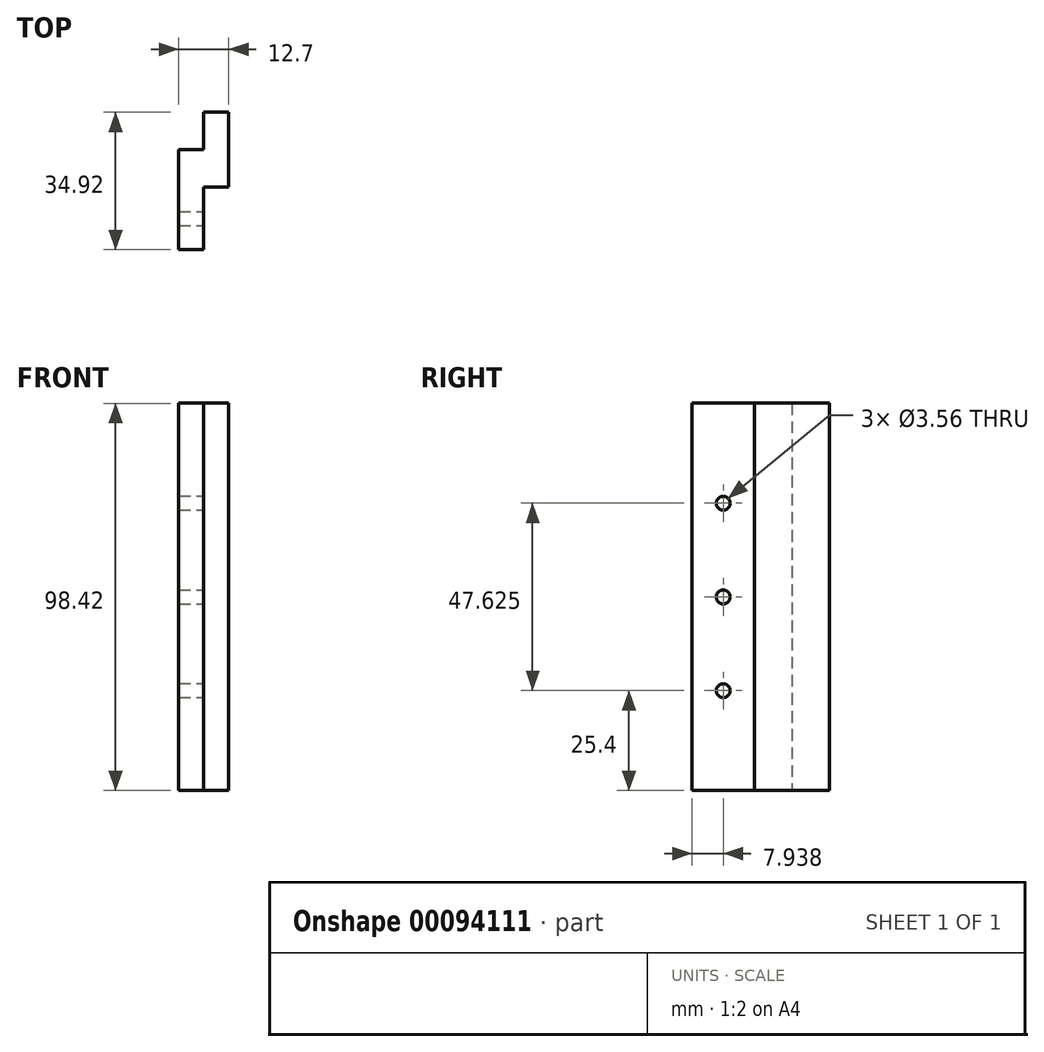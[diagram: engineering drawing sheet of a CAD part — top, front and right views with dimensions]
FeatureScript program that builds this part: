
annotation { "Feature Type Name" : "Feature", "Feature Type Description" : "" }
export const myFeature = defineFeature(function(context is Context, id is Id, definition is map)
    precondition{}
    {
        {
            var Q0;
            Q0=qCreatedBy(makeId("Top.planeOp"),FACE);
            var sketch = newSketch(context, id + "F0", { "sketchPlane" : qUnion([Q0])});
            skLineSegment(sketch, "E0.bottom", {"start": v(0, 0) * mm, "end": v(6.35, 0) * mm});
            skLineSegment(sketch, "E0.top", {"start": v(0, 25.4) * mm, "end": v(6.35, 25.4) * mm});
            skLineSegment(sketch, "E0.left", {"start": v(0, 0) * mm, "end": v(0, 25.4) * mm});
            skLineSegment(sketch, "E0.right", {"start": v(6.35, 0) * mm, "end": v(6.35, 25.4) * mm});
            skLineSegment(sketch, "E1.bottom", {"start": v(6.35, 15.88) * mm, "end": v(12.7, 15.88) * mm});
            skLineSegment(sketch, "E1.top", {"start": v(6.35, 34.93) * mm, "end": v(12.7, 34.93) * mm});
            skLineSegment(sketch, "E1.left", {"start": v(6.35, 15.88) * mm, "end": v(6.35, 34.93) * mm});
            skLineSegment(sketch, "E1.right", {"start": v(12.7, 15.88) * mm, "end": v(12.7, 34.93) * mm});
            skSolve(sketch);
        }
        {
            var Q0;
            {var subQ3=sQuery(id+"F0.wireOp",EDGE,"E1.bottom");Q0=makeQuery(id+"F0.imprint","IMPRINT",FACE,{"disambiguationData":[TD([[makeQuery(id+"F0.imprint","IMPRINT",EDGE,{"derivedFrom":subQ3}),1.0]])]});}
            var Q1;
            Q1=makeQuery(id+"F0.imprint","IMPRINT",FACE,{"disambiguationData":[TD([[makeQuery(id+"F0.imprint","IMPRINT",EDGE,{"derivedFrom":sQuery(id+"F0.wireOp",EDGE,"E0.bottom")}),1.0]])]});
            extrude(context, id + "F1", {"entities" : qUnion([Q0, Q1]), "depth" : 98.42 * mm});
        }
        {
            var Q0;
            Q0=makeQuery(id+"F1.opExtrude","SWEPT_FACE",FACE,{"disambiguationData":[OSD([sQuery(id+"F0.wireOp",EDGE,"E0.right")])]});
            var sketch = newSketch(context, id + "F2", { "sketchPlane" : qUnion([Q0])});
            skLineSegment(sketch, "E2", {"start": v(7.94, 98.43) * mm, "end": v(7.94, 0) * mm, "construction": true});
            skCircle(sketch, "E3", {"center": v(7.94, 73.03) * mm, "radius": 1.78 * mm});
            skCircle(sketch, "E4", {"center": v(7.94, 49.21) * mm, "radius": 1.78 * mm});
            skCircle(sketch, "E5", {"center": v(7.94, 25.4) * mm, "radius": 1.78 * mm});
            skSolve(sketch);
        }
        {
            var Q0;
            Q0=makeQuery(id+"F2.imprint","IMPRINT",FACE,{"disambiguationData":[TD([[makeQuery(id+"F2.imprint","IMPRINT",EDGE,{"derivedFrom":sQuery(id+"F2.wireOp",EDGE,"E3")}),1.0]])]});
            var Q1;
            Q1=makeQuery(id+"F2.imprint","IMPRINT",FACE,{"disambiguationData":[TD([[makeQuery(id+"F2.imprint","IMPRINT",EDGE,{"derivedFrom":sQuery(id+"F2.wireOp",EDGE,"E4")}),1.0]])]});
            var Q2;
            Q2=makeQuery(id+"F2.imprint","IMPRINT",FACE,{"disambiguationData":[TD([[makeQuery(id+"F2.imprint","IMPRINT",EDGE,{"derivedFrom":sQuery(id+"F2.wireOp",EDGE,"E5")}),1.0]])]});
            extrude(context, id + "F3", {"entities" : qUnion([Q0, Q1, Q2]), "operationType" : NewBodyOperationType.REMOVE, "oppositeDirection" : true, "depth" : 25.4 * mm});
        }
    });
